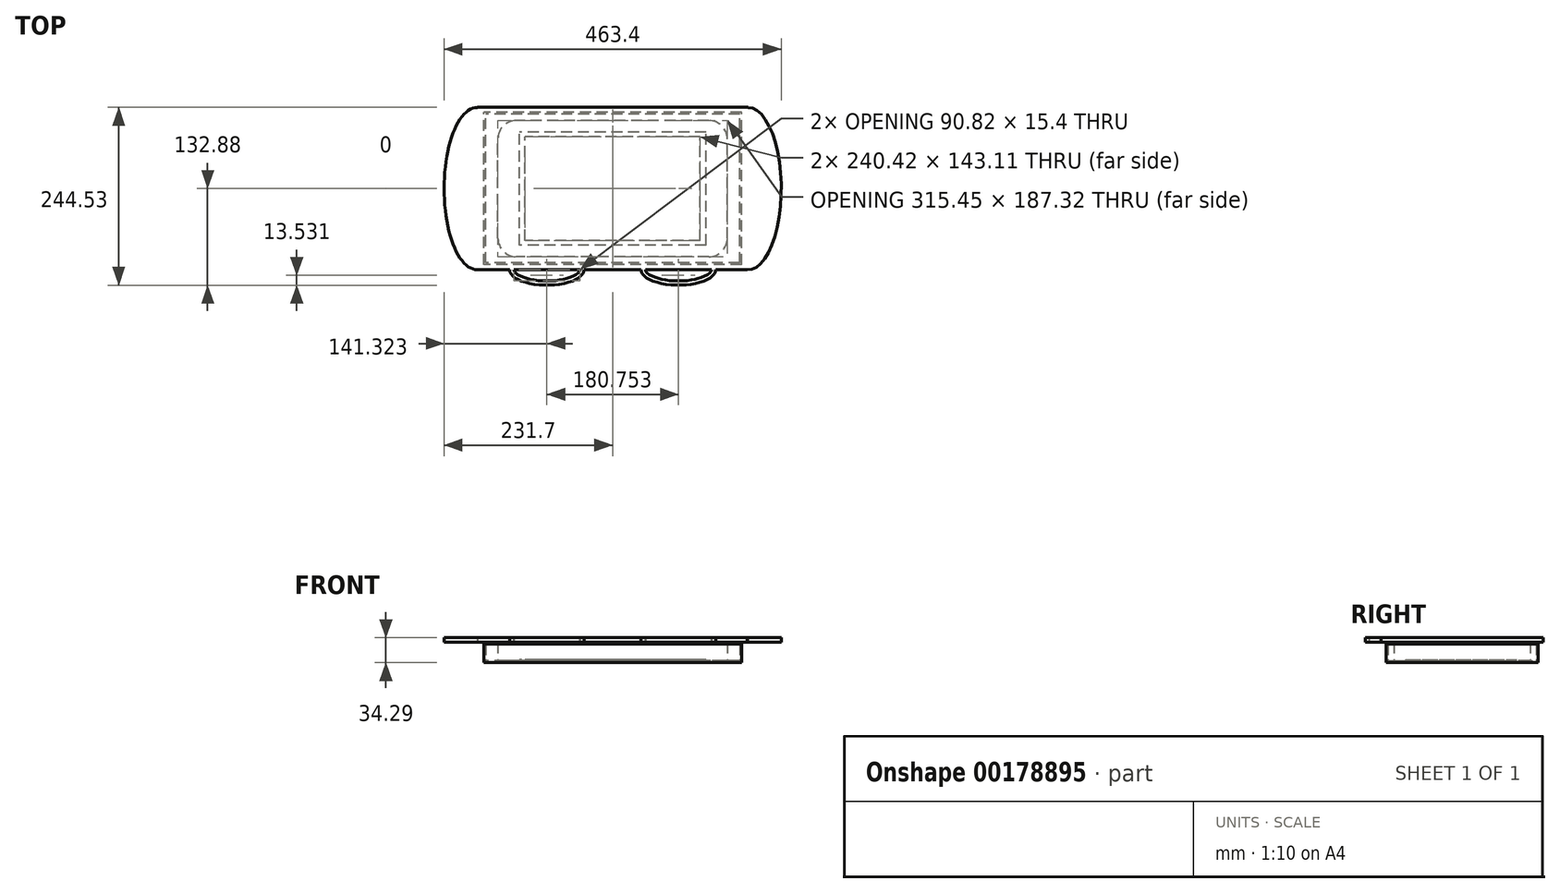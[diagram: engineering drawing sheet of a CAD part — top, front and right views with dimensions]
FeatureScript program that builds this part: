
annotation { "Feature Type Name" : "Feature", "Feature Type Description" : "" }
export const myFeature = defineFeature(function(context is Context, id is Id, definition is map)
    precondition{}
    {
        {
            var Q0;
            Q0=qCreatedBy(makeId("Top.planeOp"),FACE);
            var sketch = newSketch(context, id + "F0", { "sketchPlane" : qUnion([Q0])});
            skLineSegment(sketch, "E0.bottom", {"start": v(177.08, -104.7) * mm, "end": v(-177.08, -104.7) * mm});
            skLineSegment(sketch, "E0.top", {"start": v(177.08, 104.7) * mm, "end": v(-177.08, 104.7) * mm});
            skLineSegment(sketch, "E0.left", {"start": v(177.08, -104.7) * mm, "end": v(177.08, 104.7) * mm});
            skLineSegment(sketch, "E0.right", {"start": v(-177.08, -104.7) * mm, "end": v(-177.08, 104.7) * mm});
            skPoint(sketch, "E0.middle", {"position": v(0, 0) * mm});
            skSolve(sketch);
        }
        {
            var Q0;
            Q0=makeQuery(id+"F0.imprint","IMPRINT",FACE,{"disambiguationData":[TD([[makeQuery(id+"F0.imprint","IMPRINT",EDGE,{"derivedFrom":sQuery(id+"F0.wireOp",EDGE,"E0.bottom")}),-1.0]])]});
            extrude(context, id + "F1", {"entities" : qUnion([Q0]), "depth" : 25.4 * mm});
        }
        {
            var Q0;
            Q0=makeQuery(id+"F1.opExtrude","CAP_FACE",FACE,{"disambiguationData":[OSD([sQuery(id+"F0.wireOp",EDGE,"E0.bottom"),sQuery(id+"F0.wireOp",EDGE,"E0.top"),sQuery(id+"F0.wireOp",EDGE,"E0.left"),sQuery(id+"F0.wireOp",EDGE,"E0.right")])],"isStart":false});
            shell(context, id + "F2", {"entities" : qUnion([Q0]), "thickness" : 2.54 * mm});
        }
        {
            var Q0;
            Q0=makeQuery(id+"F2.opShell","OFFSET_FACE",FACE,{"disambiguationData":[OSD([sQuery(id+"F0.wireOp",EDGE,"E0.bottom"),sQuery(id+"F0.wireOp",EDGE,"E0.top"),sQuery(id+"F0.wireOp",EDGE,"E0.left"),sQuery(id+"F0.wireOp",EDGE,"E0.right")])]});
            var sketch = newSketch(context, id + "F3", { "sketchPlane" : qUnion([Q0])});
            skLineSegment(sketch, "E1.bottom", {"start": v(120.2, -71.55) * mm, "end": v(-120.2, -71.55) * mm});
            skLineSegment(sketch, "E1.top", {"start": v(120.2, 71.55) * mm, "end": v(-120.2, 71.55) * mm});
            skLineSegment(sketch, "E1.left", {"start": v(120.2, -71.55) * mm, "end": v(120.2, 71.55) * mm});
            skLineSegment(sketch, "E1.right", {"start": v(-120.2, -71.55) * mm, "end": v(-120.2, 71.55) * mm});
            skPoint(sketch, "E1.middle", {"position": v(0, 0) * mm});
            skSolve(sketch);
        }
        {
            var Q0;
            Q0=makeQuery(id+"F3.imprint","IMPRINT",FACE,{"disambiguationData":[TD([[makeQuery(id+"F3.imprint","IMPRINT",EDGE,{"derivedFrom":sQuery(id+"F3.wireOp",EDGE,"E1.bottom")}),-1.0]])]});
            extrude(context, id + "F4", {"entities" : qUnion([Q0]), "operationType" : NewBodyOperationType.REMOVE, "oppositeDirection" : true, "depth" : 25.4 * mm});
        }
        {
            var Q0;
            Q0=makeQuery(id+"F2.opShell","OFFSET_FACE",FACE,{"disambiguationData":[OSD([sQuery(id+"F0.wireOp",EDGE,"E0.bottom"),sQuery(id+"F0.wireOp",EDGE,"E0.top"),sQuery(id+"F0.wireOp",EDGE,"E0.left"),sQuery(id+"F0.wireOp",EDGE,"E0.right")])]});
            var sketch = newSketch(context, id + "F5", { "sketchPlane" : qUnion([Q0])});
            skLineSegment(sketch, "E2.bottom", {"start": v(128.37, -77.67) * mm, "end": v(-128.37, -77.67) * mm});
            skLineSegment(sketch, "E2.top", {"start": v(128.37, 77.67) * mm, "end": v(-128.37, 77.67) * mm});
            skLineSegment(sketch, "E2.left", {"start": v(128.37, -77.67) * mm, "end": v(128.37, 77.67) * mm});
            skLineSegment(sketch, "E2.right", {"start": v(-128.37, -77.67) * mm, "end": v(-128.37, 77.67) * mm});
            skPoint(sketch, "E2.middle", {"position": v(0, 0) * mm});
            skSolve(sketch);
        }
        {
            var Q0;
            Q0=makeQuery(id+"F5.imprint","IMPRINT",FACE,{"disambiguationData":[TD([[makeQuery(id+"F5.imprint","IMPRINT",EDGE,{"derivedFrom":sQuery(id+"F5.wireOp",EDGE,"E2.bottom")}),-1.0]])]});
            var Q1;
            Q1=makeQuery(id+"F5.imprint","IMPRINT",FACE,{"disambiguationData":[TD([[makeQuery(id+"F5.imprint","IMPRINT",EDGE,{"derivedFrom":makeQuery(id+"F4.boolean.opBoolean","COPY",EDGE,{"derivedFrom":makeQuery(id+"F4.opExtrude","CAP_EDGE",EDGE,{"disambiguationData":[OSD([sQuery(id+"F3.wireOp",EDGE,"E1.bottom")])],"isStart":true})})}),-1.0]])]});
            extrude(context, id + "F6", {"entities" : qUnion([Q0, Q1]), "depth" : 1.27 * mm});
        }
        {
            var Q0;
            Q0=makeQuery(id+"F2.opShell","OFFSET_FACE",FACE,{"disambiguationData":[OSD([sQuery(id+"F0.wireOp",EDGE,"E0.bottom"),sQuery(id+"F0.wireOp",EDGE,"E0.top"),sQuery(id+"F0.wireOp",EDGE,"E0.left"),sQuery(id+"F0.wireOp",EDGE,"E0.right")])]});
            var sketch = newSketch(context, id + "F7", { "sketchPlane" : qUnion([Q0])});
            skLineSegment(sketch, "E3.bottom", {"start": v(132.32, -93.66) * mm, "end": v(-132.32, -93.66) * mm});
            skLineSegment(sketch, "E3.top", {"start": v(132.32, 93.66) * mm, "end": v(-132.32, 93.66) * mm});
            skLineSegment(sketch, "E3.left", {"start": v(157.72, -68.26) * mm, "end": v(157.72, 68.26) * mm});
            skLineSegment(sketch, "E3.right", {"start": v(-157.72, -68.26) * mm, "end": v(-157.72, 68.26) * mm});
            skPoint(sketch, "E3.middle", {"position": v(0, 0) * mm});
            skPoint(sketch, "E4.visualSharp", {"position": v(-157.72, -93.66) * mm});
            skArc(sketch, "E4.filletArc", {"start": v(-157.72, -68.26) * mm, "mid": v(-150.28, -86.22) * mm, "end": v(-132.32, -93.66) * mm});
            skPoint(sketch, "E5.visualSharp", {"position": v(-157.72, 93.66) * mm});
            skArc(sketch, "E5.filletArc", {"start": v(-132.32, 93.66) * mm, "mid": v(-150.28, 86.22) * mm, "end": v(-157.72, 68.26) * mm});
            skPoint(sketch, "E6.visualSharp", {"position": v(157.72, 93.66) * mm});
            skArc(sketch, "E6.filletArc", {"start": v(157.72, 68.26) * mm, "mid": v(150.28, 86.22) * mm, "end": v(132.32, 93.66) * mm});
            skPoint(sketch, "E7.visualSharp", {"position": v(157.72, -93.66) * mm});
            skArc(sketch, "E7.filletArc", {"start": v(132.32, -93.66) * mm, "mid": v(150.28, -86.22) * mm, "end": v(157.72, -68.26) * mm});
            skLineSegment(sketch, "E8.bottom", {"start": v(174.54, -102.16) * mm, "end": v(-174.54, -102.16) * mm});
            skLineSegment(sketch, "E8.top", {"start": v(174.54, 102.16) * mm, "end": v(-174.54, 102.16) * mm});
            skLineSegment(sketch, "E8.left", {"start": v(174.54, -102.16) * mm, "end": v(174.54, 102.16) * mm});
            skLineSegment(sketch, "E8.right", {"start": v(-174.54, -102.16) * mm, "end": v(-174.54, 102.16) * mm});
            skSolve(sketch);
        }
        {
            var Q0;
            Q0=makeQuery(id+"F7.imprint","IMPRINT",FACE,{"disambiguationData":[TD([[makeQuery(id+"F7.imprint","IMPRINT",EDGE,{"derivedFrom":sQuery(id+"F7.wireOp",EDGE,"E3.bottom")}),1.0]])]});
            extrude(context, id + "F8", {"entities" : qUnion([Q0]), "depth" : 25.4 * mm});
        }
        {
            var Q0;
            Q0=makeQuery(id+"F8.opExtrude","CAP_FACE",FACE,{"disambiguationData":[OSD([sQuery(id+"F7.wireOp",EDGE,"E3.bottom"),sQuery(id+"F7.wireOp",EDGE,"E3.top"),sQuery(id+"F7.wireOp",EDGE,"E3.left"),sQuery(id+"F7.wireOp",EDGE,"E3.right"),sQuery(id+"F7.wireOp",EDGE,"E4.filletArc"),sQuery(id+"F7.wireOp",EDGE,"E5.filletArc"),sQuery(id+"F7.wireOp",EDGE,"E6.filletArc"),sQuery(id+"F7.wireOp",EDGE,"E7.filletArc"),sQuery(id+"F7.wireOp",EDGE,"E8.bottom"),sQuery(id+"F7.wireOp",EDGE,"E8.top"),sQuery(id+"F7.wireOp",EDGE,"E8.left"),sQuery(id+"F7.wireOp",EDGE,"E8.right")])],"isStart":false});
            var sketch = newSketch(context, id + "F9", { "sketchPlane" : qUnion([Q0])});
            skLineSegment(sketch, "E9.bottom", {"start": v(186.12, -111.65) * mm, "end": v(141.63, -111.65) * mm});
            skLineSegment(sketch, "E9.top", {"start": v(186.12, 111.65) * mm, "end": v(-186.12, 111.65) * mm});
            skLineSegment(sketch, "E9.left", {"start": v(186.12, -95.68) * mm, "end": v(186.12, 95.61) * mm});
            skLineSegment(sketch, "E9.right", {"start": v(-186.12, -95.65) * mm, "end": v(-186.12, 95.65) * mm});
            skPoint(sketch, "E9.middle", {"position": v(0, 0) * mm});
            skEllipticalArc(sketch, "E10", {});
            skEllipticalArc(sketch, "E11", {});
            skFitSpline(sketch, "E12.0", {"points": [v(-186.44, -95.64) * mm, v(-186.12, -95.65) * mm, v(-185.8, -95.64) * mm, v(-185.42, -95.57) * mm, v(-184.91, -95.42) * mm, v(-184.03, -95.05) * mm, v(-182.51, -94.15) * mm, v(-180.13, -92.1) * mm, v(-177.4, -88.96) * mm, v(-174.97, -85.42) * mm, v(-173.01, -82.06) * mm, v(-171.55, -79.27) * mm, v(-170.11, -76.23) * mm, v(-168.7, -72.94) * mm, v(-167.33, -69.42) * mm, v(-166.03, -65.71) * mm, v(-164.8, -61.82) * mm, v(-163.24, -56.41) * mm, v(-161.49, -49.26) * mm, v(-159.73, -40.13) * mm, v(-158.33, -30.56) * mm, v(-157.48, -22.28) * mm, v(-157, -15.52) * mm, v(-156.74, -10.4) * mm, v(-156.6, -6.08) * mm, v(-156.55, -2.61) * mm, v(-156.54, 0) * mm, v(-156.55, 2.61) * mm, v(-156.6, 6.08) * mm, v(-156.74, 10.4) * mm, v(-157, 15.52) * mm, v(-157.48, 22.28) * mm, v(-158.33, 30.56) * mm, v(-159.73, 40.13) * mm, v(-161.49, 49.26) * mm, v(-163.24, 56.41) * mm, v(-164.8, 61.82) * mm, v(-166.03, 65.71) * mm, v(-167.33, 69.42) * mm, v(-168.7, 72.94) * mm, v(-170.11, 76.23) * mm, v(-171.55, 79.27) * mm, v(-173.01, 82.06) * mm, v(-174.97, 85.42) * mm, v(-177.4, 88.96) * mm, v(-180.13, 92.1) * mm, v(-182.51, 94.15) * mm, v(-184.03, 95.05) * mm, v(-184.91, 95.42) * mm, v(-185.42, 95.57) * mm, v(-185.8, 95.64) * mm, v(-186.12, 95.65) * mm, v(-186.44, 95.64) * mm, v(-186.82, 95.57) * mm, v(-187.33, 95.42) * mm, v(-188.2, 95.05) * mm, v(-189.72, 94.15) * mm, v(-192.1, 92.1) * mm, v(-194.84, 88.96) * mm, v(-197.27, 85.42) * mm, v(-199.22, 82.06) * mm, v(-200.68, 79.27) * mm, v(-202.13, 76.23) * mm, v(-203.54, 72.94) * mm, v(-204.9, 69.42) * mm, v(-206.2, 65.71) * mm, v(-207.45, 61.82) * mm, v(-209, 56.41) * mm, v(-210.75, 49.26) * mm, v(-212.5, 40.13) * mm, v(-213.9, 30.56) * mm, v(-214.76, 22.28) * mm, v(-215.24, 15.52) * mm, v(-215.5, 10.4) * mm, v(-215.63, 6.08) * mm, v(-215.69, 2.61) * mm, v(-215.7, 0) * mm, v(-215.69, -2.61) * mm, v(-215.63, -6.08) * mm, v(-215.5, -10.4) * mm, v(-215.24, -15.52) * mm, v(-214.76, -22.28) * mm, v(-213.9, -30.56) * mm, v(-212.5, -40.13) * mm, v(-210.75, -49.26) * mm, v(-209, -56.41) * mm, v(-207.45, -61.82) * mm, v(-206.2, -65.71) * mm, v(-204.9, -69.42) * mm, v(-203.54, -72.94) * mm, v(-202.13, -76.23) * mm, v(-200.68, -79.27) * mm, v(-199.22, -82.06) * mm, v(-197.27, -85.42) * mm, v(-194.84, -88.96) * mm, v(-192.1, -92.1) * mm, v(-189.72, -94.15) * mm, v(-188.2, -95.05) * mm, v(-187.33, -95.42) * mm, v(-186.82, -95.57) * mm, v(-186.44, -95.64) * mm, v(-186.12, -95.65) * mm, v(-185.8, -95.64) * mm]});
            skLineSegment(sketch, "E13", {"start": v(0, 0) * mm, "end": v(0, 136.24) * mm, "construction": true});
            skPoint(sketch, "E13.endSnap0", {"position": v(0, 111.65) * mm});
            skEllipticalArc(sketch, "E14.MirrorC", {});
            skFitSpline(sketch, "E15.0", {"points": [v(185.8, -95.67) * mm, v(186.12, -95.69) * mm, v(186.44, -95.67) * mm, v(186.82, -95.6) * mm, v(187.33, -95.45) * mm, v(188.2, -95.09) * mm, v(189.72, -94.19) * mm, v(192.1, -92.14) * mm, v(194.84, -89) * mm, v(197.27, -85.46) * mm, v(199.22, -82.1) * mm, v(200.68, -79.3) * mm, v(202.13, -76.27) * mm, v(203.54, -72.97) * mm, v(204.9, -69.46) * mm, v(206.2, -65.75) * mm, v(207.45, -61.86) * mm, v(209, -56.45) * mm, v(210.75, -49.3) * mm, v(212.5, -40.17) * mm, v(213.9, -30.6) * mm, v(214.76, -22.32) * mm, v(215.24, -15.56) * mm, v(215.5, -10.43) * mm, v(215.63, -6.12) * mm, v(215.69, -2.65) * mm, v(215.7, -0.04) * mm, v(215.69, 2.58) * mm, v(215.63, 6.05) * mm, v(215.5, 10.36) * mm, v(215.24, 15.49) * mm, v(214.76, 22.25) * mm, v(213.9, 30.53) * mm, v(212.5, 40.1) * mm, v(210.75, 49.22) * mm, v(209, 56.38) * mm, v(207.45, 61.79) * mm, v(206.2, 65.68) * mm, v(204.9, 69.38) * mm, v(203.54, 72.9) * mm, v(202.13, 76.2) * mm, v(200.68, 79.24) * mm, v(199.22, 82.02) * mm, v(197.27, 85.39) * mm, v(194.84, 88.92) * mm, v(192.1, 92.06) * mm, v(189.72, 94.12) * mm, v(188.2, 95.01) * mm, v(187.33, 95.38) * mm, v(186.82, 95.53) * mm, v(186.44, 95.6) * mm, v(186.12, 95.62) * mm, v(185.8, 95.6) * mm, v(185.42, 95.53) * mm, v(184.91, 95.38) * mm, v(184.03, 95.01) * mm, v(182.51, 94.12) * mm, v(180.13, 92.06) * mm, v(177.4, 88.92) * mm, v(174.97, 85.39) * mm, v(173.01, 82.02) * mm, v(171.55, 79.24) * mm, v(170.11, 76.2) * mm, v(168.7, 72.9) * mm, v(167.33, 69.38) * mm, v(166.03, 65.68) * mm, v(164.8, 61.79) * mm, v(163.24, 56.38) * mm, v(161.49, 49.22) * mm, v(159.73, 40.1) * mm, v(158.33, 30.53) * mm, v(157.48, 22.25) * mm, v(157, 15.49) * mm, v(156.74, 10.36) * mm, v(156.6, 6.05) * mm, v(156.55, 2.58) * mm, v(156.54, -0.04) * mm, v(156.55, -2.65) * mm, v(156.6, -6.12) * mm, v(156.74, -10.43) * mm, v(157, -15.56) * mm, v(157.48, -22.32) * mm, v(158.33, -30.6) * mm, v(159.73, -40.17) * mm, v(161.49, -49.3) * mm, v(163.24, -56.45) * mm, v(164.8, -61.86) * mm, v(166.03, -65.75) * mm, v(167.33, -69.46) * mm, v(168.7, -72.97) * mm, v(170.11, -76.27) * mm, v(171.55, -79.3) * mm, v(173.01, -82.1) * mm, v(174.97, -85.46) * mm, v(177.4, -89) * mm, v(180.13, -92.14) * mm, v(182.51, -94.19) * mm, v(184.03, -95.09) * mm, v(184.91, -95.45) * mm, v(185.42, -95.6) * mm, v(185.8, -95.67) * mm, v(186.12, -95.69) * mm, v(186.44, -95.67) * mm]});
            skLineSegment(sketch, "E16.trimOffspring", {"start": v(186.12, 111.61) * mm, "end": v(186.12, 111.65) * mm});
            skLineSegment(sketch, "E17.trimOffspring", {"start": v(-186.12, 111.61) * mm, "end": v(-186.12, 111.65) * mm});
            skEllipticalArc(sketch, "E18", {});
            skEllipticalArc(sketch, "E19.MirrorC", {});
            skFitSpline(sketch, "E20.0", {"points": [v(-135.78, -111.65) * mm, v(-135.78, -111.88) * mm, v(-135.73, -112.35) * mm, v(-135.43, -113.23) * mm, v(-134.78, -114.33) * mm, v(-133.68, -115.62) * mm, v(-132.08, -117.03) * mm, v(-129.28, -118.98) * mm, v(-125.57, -120.86) * mm, v(-121.08, -122.55) * mm, v(-117.97, -123.5) * mm, v(-115.33, -124.2) * mm, v(-112.59, -124.84) * mm, v(-107.6, -125.82) * mm, v(-101.5, -126.59) * mm, v(-95.98, -126.93) * mm, v(-92.78, -127.02) * mm, v(-90.38, -127.05) * mm, v(-87.97, -127.02) * mm, v(-84.78, -126.93) * mm, v(-79.25, -126.59) * mm, v(-73.16, -125.82) * mm, v(-68.16, -124.84) * mm, v(-65.42, -124.2) * mm, v(-62.78, -123.5) * mm, v(-59.68, -122.55) * mm, v(-55.19, -120.86) * mm, v(-51.47, -118.98) * mm, v(-48.67, -117.03) * mm, v(-47.07, -115.62) * mm, v(-45.97, -114.33) * mm, v(-45.32, -113.23) * mm, v(-45.02, -112.35) * mm, v(-44.97, -111.88) * mm, v(-44.97, -111.65) * mm]});
            skFitSpline(sketch, "E21.0", {"points": [v(44.97, -111.65) * mm, v(44.97, -111.88) * mm, v(45.02, -112.35) * mm, v(45.32, -113.23) * mm, v(45.97, -114.33) * mm, v(47.07, -115.62) * mm, v(48.67, -117.03) * mm, v(51.47, -118.98) * mm, v(55.19, -120.86) * mm, v(59.68, -122.55) * mm, v(62.78, -123.5) * mm, v(65.42, -124.2) * mm, v(68.16, -124.84) * mm, v(73.16, -125.82) * mm, v(79.25, -126.59) * mm, v(84.78, -126.93) * mm, v(87.97, -127.02) * mm, v(90.38, -127.05) * mm, v(92.78, -127.02) * mm, v(95.98, -126.93) * mm, v(101.5, -126.59) * mm, v(107.6, -125.82) * mm, v(112.59, -124.84) * mm, v(115.33, -124.2) * mm, v(117.97, -123.5) * mm, v(121.08, -122.55) * mm, v(125.57, -120.86) * mm, v(129.28, -118.98) * mm, v(132.08, -117.03) * mm, v(133.68, -115.62) * mm, v(134.78, -114.33) * mm, v(135.43, -113.23) * mm, v(135.73, -112.35) * mm, v(135.78, -111.88) * mm, v(135.78, -111.65) * mm]});
            skLineSegment(sketch, "E22.trimOffspring", {"start": v(-141.63, -111.65) * mm, "end": v(-186.12, -111.65) * mm});
            skLineSegment(sketch, "E23.trimOffspring", {"start": v(-44.97, -111.65) * mm, "end": v(-135.78, -111.65) * mm});
            skLineSegment(sketch, "E24.trimOffspring", {"start": v(39.13, -111.65) * mm, "end": v(-39.13, -111.65) * mm});
            skLineSegment(sketch, "E25.trimOffspring", {"start": v(135.78, -111.65) * mm, "end": v(44.97, -111.65) * mm});
            const initialGuessF9  = {"E10": [-0.18611861765384674, 0, 0, -1, 0.1116495281457901, 0.04557750202425955, 3.141592653589793, 0], "E11": [0.18611861092772636, -3.5519781260105346e-05, 0, -1, 0.1116495281457901, 0.04557750202425955, 6.257960189117566, 3.1415925060143417], "E14.MirrorC": [-0.18611861092772636, -3.551978126018941e-05, 0, -1, 0.1116495281457901, 0.04557750202425955, 3.141592653589793, 0.025225118062051764], "E18": [-0.0903766006231308, -0.1116495281457901, 1, 0, 0.0512499064207077, 0.02123292508782751, 3.141592653589793, 0], "E19.MirrorC": [0.0903766006231308, -0.1116495281457901, -1, 0, 0.0512499064207077, 0.02123292508782751, 0, 3.141592653589793]};
            skSetInitialGuess(sketch, initialGuessF9);
            skSolve(sketch);
        }
        {
            var Q0;
            Q0=makeQuery(id+"F9.imprint","IMPRINT",FACE,{"disambiguationData":[TD([[makeQuery(id+"F9.imprint","IMPRINT",EDGE,{"derivedFrom":sQuery(id+"F9.wireOp",EDGE,"E9.top")}),1.0]])]});
            var Q1;
            Q1=makeQuery(id+"F9.imprint","IMPRINT",FACE,{"disambiguationData":[TD([[makeQuery(id+"F9.imprint","IMPRINT",EDGE,{"derivedFrom":makeQuery(id+"F8.opExtrude","CAP_EDGE",EDGE,{"disambiguationData":[OSD([sQuery(id+"F7.wireOp",EDGE,"E3.bottom")])],"isStart":false})}),1.0]])]});
            var Q2;
            Q2=makeQuery(id+"F9.imprint","IMPRINT",FACE,{"disambiguationData":[TD([[makeQuery(id+"F9.imprint","IMPRINT",EDGE,{"derivedFrom":makeQuery(id+"F8.opExtrude","CAP_EDGE",EDGE,{"disambiguationData":[OSD([sQuery(id+"F7.wireOp",EDGE,"E3.bottom")])],"isStart":false})}),-1.0]])]});
            extrude(context, id + "F10", {"entities" : qUnion([Q0, Q1, Q2]), "depth" : 6.35 * mm});
        }
    });
